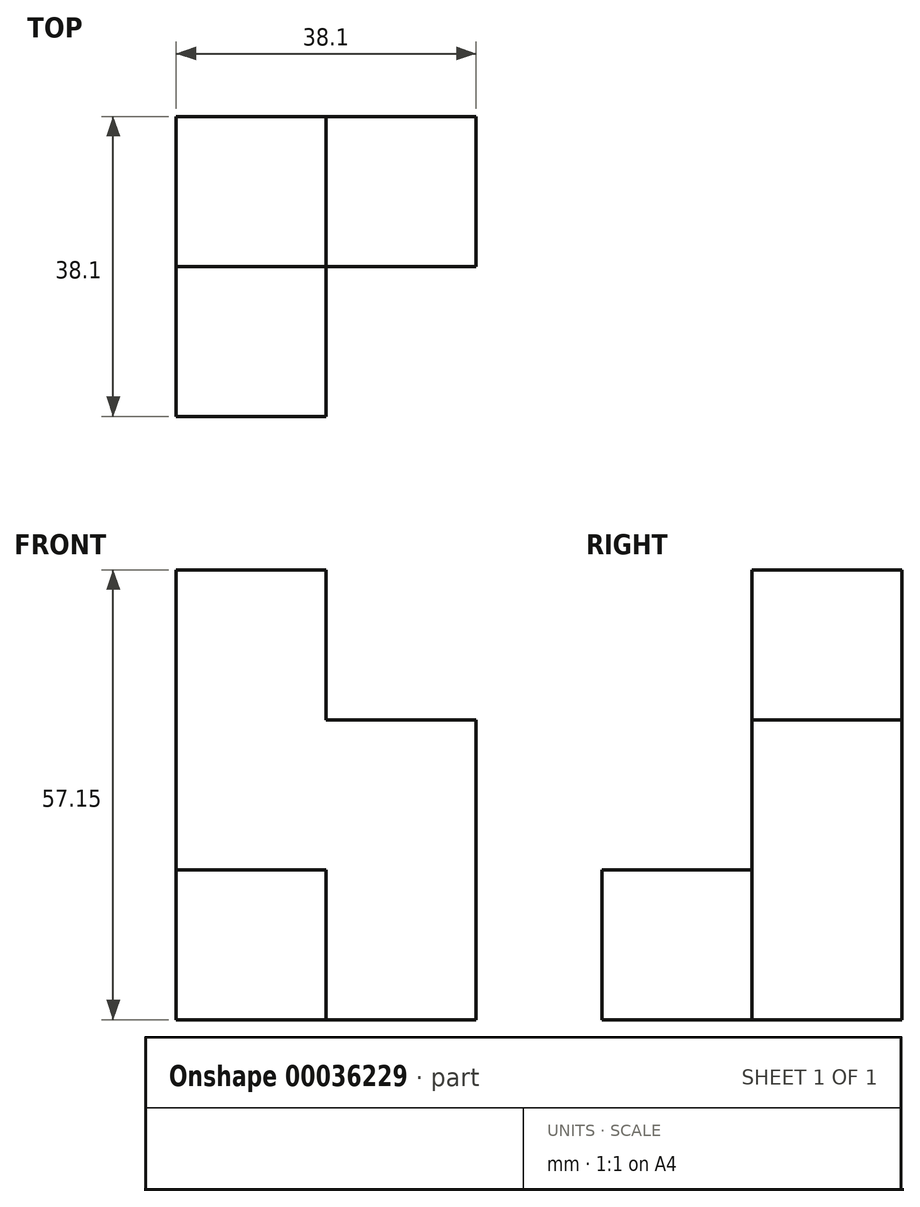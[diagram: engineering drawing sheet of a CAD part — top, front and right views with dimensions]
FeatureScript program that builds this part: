
annotation { "Feature Type Name" : "Feature", "Feature Type Description" : "" }
export const myFeature = defineFeature(function(context is Context, id is Id, definition is map)
    precondition{}
    {
        {
            var Q0;
            Q0=qCreatedBy(makeId("Top.planeOp"),FACE);
            var sketch = newSketch(context, id + "F0", { "sketchPlane" : qUnion([Q0])});
            skLineSegment(sketch, "E0.bottom", {"start": v(-70.79, -69.36) * mm, "end": v(-51.74, -69.36) * mm});
            skLineSegment(sketch, "E0.top", {"start": v(-70.79, -50.31) * mm, "end": v(-51.74, -50.31) * mm});
            skLineSegment(sketch, "E0.left", {"start": v(-70.79, -69.36) * mm, "end": v(-70.79, -50.31) * mm});
            skLineSegment(sketch, "E0.right", {"start": v(-51.74, -69.36) * mm, "end": v(-51.74, -50.31) * mm});
            skSolve(sketch);
        }
        {
            var Q0;
            Q0 = qSketchRegion(id + "F0", true);
            extrude(context, id + "F1", {"entities" : qUnion([Q0]), "depth" : 19.05 * mm});
        }
        {
            var Q0;
            Q0=makeQuery(id+"F1.opExtrude","SWEPT_FACE",FACE,{"disambiguationData":[OSD([sQuery(id+"F0.wireOp",EDGE,"E0.right")])]});
            var sketch = newSketch(context, id + "F2", { "sketchPlane" : qUnion([Q0])});
            skLineSegment(sketch, "E1.bottom", {"start": v(-50.31, 19.05) * mm, "end": v(-69.36, 19.05) * mm});
            skLineSegment(sketch, "E1.top", {"start": v(-50.31, 0) * mm, "end": v(-69.36, 0) * mm});
            skLineSegment(sketch, "E1.left", {"start": v(-50.31, 19.05) * mm, "end": v(-50.31, 0) * mm});
            skLineSegment(sketch, "E1.right", {"start": v(-69.36, 19.05) * mm, "end": v(-69.36, 0) * mm});
            skSolve(sketch);
        }
        {
            var Q0;
            Q0 = qSketchRegion(id + "F2", true);
            extrude(context, id + "F3", {"entities" : qUnion([Q0]), "operationType" : NewBodyOperationType.ADD, "depth" : 19.05 * mm});
        }
        {
            var Q0;
            Q0=makeQuery(id+"F3.boolean.opBoolean","MERGE",FACE,{"derivedFrom":[makeQuery(id+"F1.opExtrude","CAP_FACE",FACE,{"disambiguationData":[OSD([sQuery(id+"F0.wireOp",EDGE,"E0.bottom"),sQuery(id+"F0.wireOp",EDGE,"E0.top"),sQuery(id+"F0.wireOp",EDGE,"E0.left"),sQuery(id+"F0.wireOp",EDGE,"E0.right")])],"isStart":false}),makeQuery(id+"F3.opExtrude","SWEPT_FACE",FACE,{"disambiguationData":[OSD([sQuery(id+"F2.wireOp",EDGE,"E1.bottom")])]})]});
            var sketch = newSketch(context, id + "F4", { "sketchPlane" : qUnion([Q0])});
            skLineSegment(sketch, "E2.bottom", {"start": v(-70.79, -50.31) * mm, "end": v(-51.74, -50.31) * mm});
            skLineSegment(sketch, "E2.top", {"start": v(-70.79, -69.36) * mm, "end": v(-51.74, -69.36) * mm});
            skLineSegment(sketch, "E2.left", {"start": v(-70.79, -50.31) * mm, "end": v(-70.79, -69.36) * mm});
            skLineSegment(sketch, "E2.right", {"start": v(-51.74, -50.31) * mm, "end": v(-51.74, -69.36) * mm});
            skSolve(sketch);
        }
        {
            var Q0;
            Q0 = qSketchRegion(id + "F4", true);
            extrude(context, id + "F5", {"entities" : qUnion([Q0]), "operationType" : NewBodyOperationType.ADD, "depth" : 19.05 * mm});
        }
        {
            var Q0;
            Q0=makeQuery(id+"F5.opExtrude","SWEPT_FACE",FACE,{"disambiguationData":[OSD([sQuery(id+"F4.wireOp",EDGE,"E2.right")])]});
            var sketch = newSketch(context, id + "F6", { "sketchPlane" : qUnion([Q0])});
            skLineSegment(sketch, "E3.bottom", {"start": v(-50.31, 38.1) * mm, "end": v(-69.36, 38.1) * mm});
            skLineSegment(sketch, "E3.top", {"start": v(-50.31, 19.05) * mm, "end": v(-69.36, 19.05) * mm});
            skLineSegment(sketch, "E3.left", {"start": v(-50.31, 38.1) * mm, "end": v(-50.31, 19.05) * mm});
            skLineSegment(sketch, "E3.right", {"start": v(-69.36, 38.1) * mm, "end": v(-69.36, 19.05) * mm});
            skSolve(sketch);
        }
        {
            var Q0;
            Q0 = qSketchRegion(id + "F6", true);
            extrude(context, id + "F7", {"entities" : qUnion([Q0]), "operationType" : NewBodyOperationType.ADD, "depth" : 19.05 * mm});
        }
        {
            var Q0;
            Q0=makeQuery(id+"F7.boolean.opBoolean","MERGE",FACE,{"derivedFrom":[makeQuery(id+"F5.opExtrude","CAP_FACE",FACE,{"disambiguationData":[OSD([sQuery(id+"F4.wireOp",EDGE,"E2.bottom"),sQuery(id+"F4.wireOp",EDGE,"E2.top"),sQuery(id+"F4.wireOp",EDGE,"E2.left"),sQuery(id+"F4.wireOp",EDGE,"E2.right")])],"isStart":false}),makeQuery(id+"F7.opExtrude","SWEPT_FACE",FACE,{"disambiguationData":[OSD([sQuery(id+"F6.wireOp",EDGE,"E3.bottom")])]})]});
            var sketch = newSketch(context, id + "F8", { "sketchPlane" : qUnion([Q0])});
            skLineSegment(sketch, "E4.bottom", {"start": v(-70.79, -50.31) * mm, "end": v(-51.74, -50.31) * mm});
            skLineSegment(sketch, "E4.top", {"start": v(-70.79, -69.36) * mm, "end": v(-51.74, -69.36) * mm});
            skLineSegment(sketch, "E4.left", {"start": v(-70.79, -50.31) * mm, "end": v(-70.79, -69.36) * mm});
            skLineSegment(sketch, "E4.right", {"start": v(-51.74, -50.31) * mm, "end": v(-51.74, -69.36) * mm});
            skSolve(sketch);
        }
        {
            var Q0;
            Q0 = qSketchRegion(id + "F8", true);
            extrude(context, id + "F9", {"entities" : qUnion([Q0]), "operationType" : NewBodyOperationType.ADD, "depth" : 19.05 * mm});
        }
        {
            var Q0;
            Q0=makeQuery(id+"F9.boolean.opBoolean","MERGE",FACE,{"derivedFrom":[makeQuery(id+"F7.boolean.opBoolean","MERGE",FACE,{"derivedFrom":[makeQuery(id+"F5.boolean.opBoolean","MERGE",FACE,{"derivedFrom":[makeQuery(id+"F3.boolean.opBoolean","MERGE",FACE,{"derivedFrom":[makeQuery(id+"F1.opExtrude","SWEPT_FACE",FACE,{"disambiguationData":[OSD([sQuery(id+"F0.wireOp",EDGE,"E0.bottom")])]}),makeQuery(id+"F3.opExtrude","SWEPT_FACE",FACE,{"disambiguationData":[OSD([sQuery(id+"F2.wireOp",EDGE,"E1.right")])]})]}),makeQuery(id+"F5.opExtrude","SWEPT_FACE",FACE,{"disambiguationData":[OSD([sQuery(id+"F4.wireOp",EDGE,"E2.top")])]})]}),makeQuery(id+"F7.opExtrude","SWEPT_FACE",FACE,{"disambiguationData":[OSD([sQuery(id+"F6.wireOp",EDGE,"E3.right")])]})]}),makeQuery(id+"F9.opExtrude","SWEPT_FACE",FACE,{"disambiguationData":[OSD([sQuery(id+"F8.wireOp",EDGE,"E4.top")])]})]});
            var sketch = newSketch(context, id + "F10", { "sketchPlane" : qUnion([Q0])});
            skLineSegment(sketch, "E5.bottom", {"start": v(-70.79, 0) * mm, "end": v(-51.74, 0) * mm});
            skLineSegment(sketch, "E5.top", {"start": v(-70.79, 19.05) * mm, "end": v(-51.74, 19.05) * mm});
            skLineSegment(sketch, "E5.left", {"start": v(-70.79, 0) * mm, "end": v(-70.79, 19.05) * mm});
            skLineSegment(sketch, "E5.right", {"start": v(-51.74, 0) * mm, "end": v(-51.74, 19.05) * mm});
            skSolve(sketch);
        }
        {
            var Q0;
            Q0 = qSketchRegion(id + "F10", true);
            extrude(context, id + "F11", {"entities" : qUnion([Q0]), "operationType" : NewBodyOperationType.ADD, "depth" : 19.05 * mm});
        }
    });
